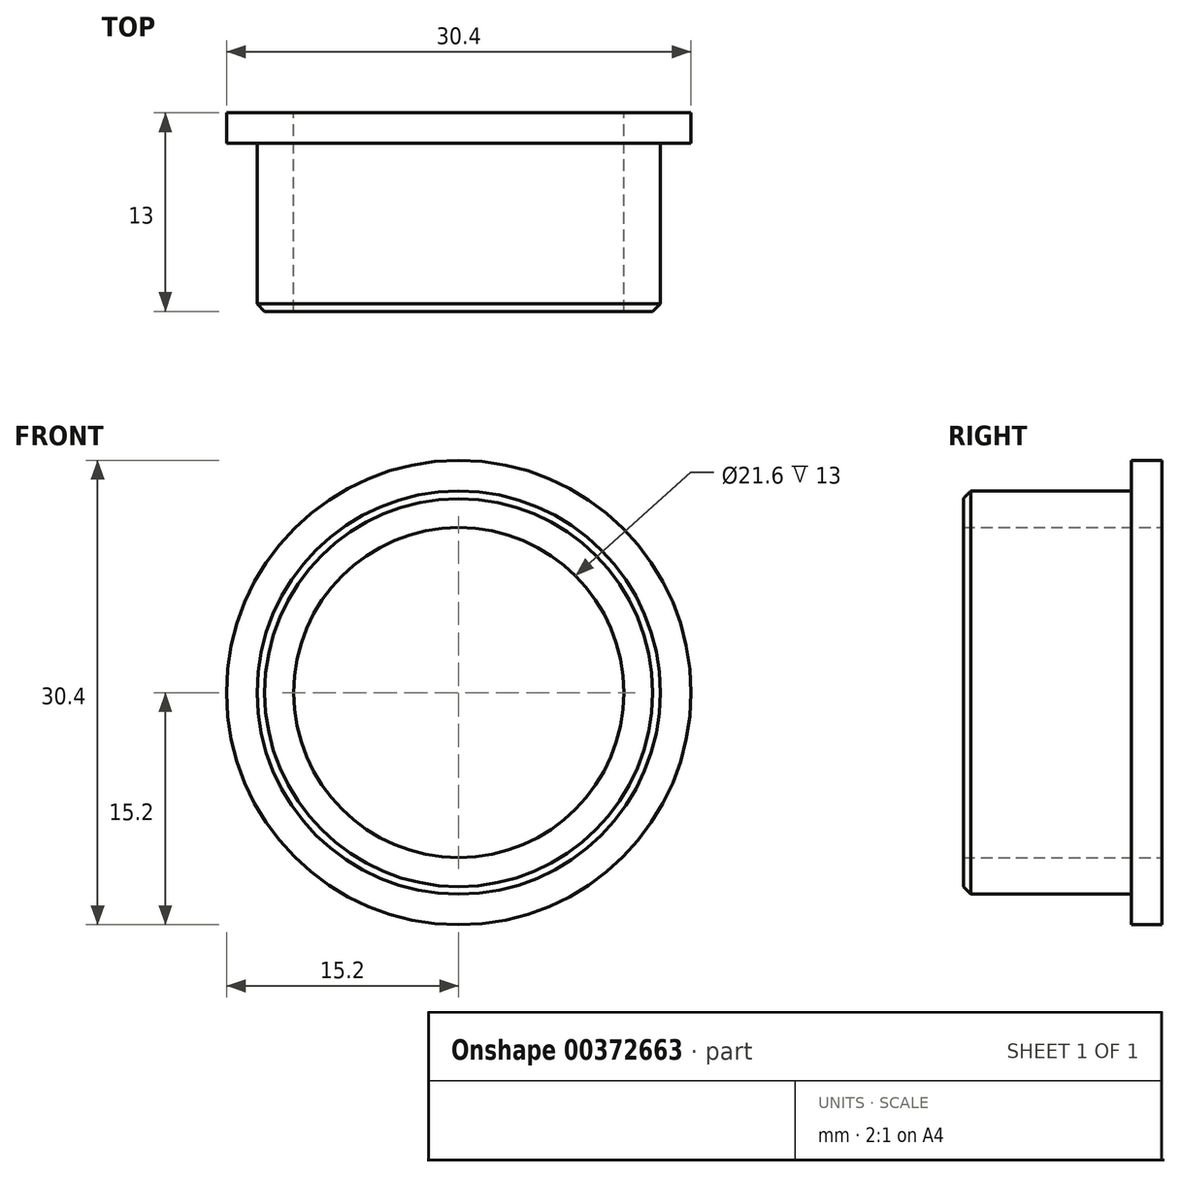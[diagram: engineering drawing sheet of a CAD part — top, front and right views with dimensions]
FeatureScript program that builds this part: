
annotation { "Feature Type Name" : "Feature", "Feature Type Description" : "" }
export const myFeature = defineFeature(function(context is Context, id is Id, definition is map)
    precondition{}
    {
        {
            var Q0;
            Q0=qCreatedBy(makeId("Top.planeOp"),FACE);
            var sketch = newSketch(context, id + "F0", { "sketchPlane" : qUnion([Q0])});
            skLineSegment(sketch, "E0", {"start": v(0, 0) * mm, "end": v(0, -13) * mm});
            skLineSegment(sketch, "E1", {"start": v(0, -13) * mm, "end": v(13.2, -13) * mm});
            skLineSegment(sketch, "E2", {"start": v(13.2, -13) * mm, "end": v(13.2, -2) * mm});
            skLineSegment(sketch, "E3", {"start": v(13.2, -2) * mm, "end": v(15.2, -2) * mm});
            skLineSegment(sketch, "E4", {"start": v(15.2, -2) * mm, "end": v(15.2, 0) * mm});
            skLineSegment(sketch, "E5", {"start": v(15.2, 0) * mm, "end": v(0, 0) * mm});
            skLineSegment(sketch, "E6", {"start": v(10.8, 0) * mm, "end": v(10.8, -13) * mm});
            skSolve(sketch);
        }
        {
            var Q0;
            {var subQ1=sQuery(id+"F0.wireOp",EDGE,"E2");Q0=makeQuery(id+"F0.imprint","IMPRINT",FACE,{"disambiguationData":[TD([[makeQuery(id+"F0.imprint","IMPRINT",EDGE,{"derivedFrom":subQ1}),1.0]])]});}
            var Q1;
            Q1=sQuery(id+"F0.wireOp",EDGE,"E0");
            revolve(context, id + "F1", {"surfaceOperationType" : NewSurfaceOperationType.NEW, "entities" : qUnion([Q0]), "axis" : qUnion([Q1]), "revolveType" : RevolveType.FULL});
        }
        {
            var Q0;
            Q0=makeQuery(id+"F1.opRevolve","SWEPT_EDGE",EDGE,{"disambiguationData":[OSD([sQuery(id+"F0.wireOp",EDGE,"E1"),sQuery(id+"F0.wireOp",EDGE,"E2")])]});
            chamfer(context, id + "F2", {"entities" : qUnion([Q0]), "width" : .5 * mm, "tangentPropagation" : true});
        }
    });
